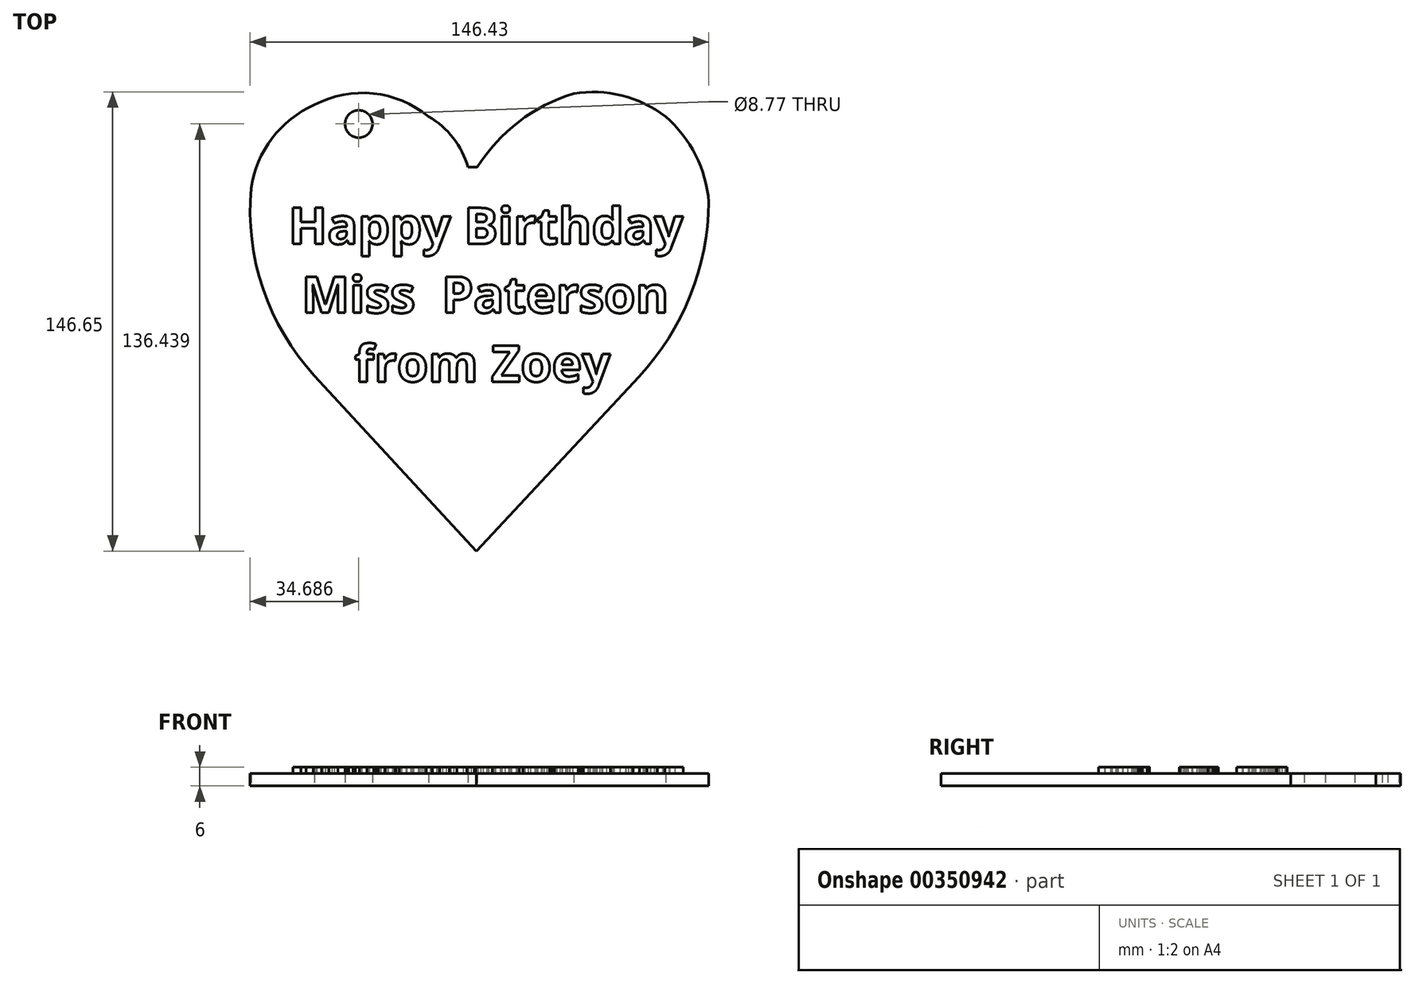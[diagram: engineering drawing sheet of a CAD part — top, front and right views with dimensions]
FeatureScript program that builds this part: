
annotation { "Feature Type Name" : "Feature", "Feature Type Description" : "" }
export const myFeature = defineFeature(function(context is Context, id is Id, definition is map)
    precondition{}
    {
        {
            var Q0;
            Q0=qCreatedBy(makeId("Top.planeOp"),FACE);
            var sketch = newSketch(context, id + "F0", { "sketchPlane" : qUnion([Q0])});
            skLineSegment(sketch, "E0", {"start": v(2.64, -78.33) * mm, "end": v(54.56, -22.56) * mm});
            skLineSegment(sketch, "E1", {"start": v(2.64, -78.33) * mm, "end": v(-49, -22.3) * mm});
            skArc(sketch, "E2", {"start": v(-69.24, 37.55) * mm, "mid": v(-65.47, 5.48) * mm, "end": v(-49, -22.3) * mm});
            skArc(sketch, "E3", {"start": v(-49, 64.25) * mm, "mid": v(-62.57, 53.52) * mm, "end": v(-69.24, 37.55) * mm});
            skArc(sketch, "E4", {"start": v(-12.62, 60.44) * mm, "mid": v(-30.23, 67.85) * mm, "end": v(-49, 64.25) * mm});
            skArc(sketch, "E5", {"start": v(0, 44.3) * mm, "mid": v(-4.71, 53.62) * mm, "end": v(-12.62, 60.44) * mm});
            skLineSegment(sketch, "E6", {"start": v(0, 44.3) * mm, "end": v(2.93, 44.3) * mm});
            skArc(sketch, "E7", {"start": v(33.73, 67.8) * mm, "mid": v(16.2, 58.84) * mm, "end": v(2.93, 44.3) * mm});
            skArc(sketch, "E8", {"start": v(63.07, 60.47) * mm, "mid": v(49.16, 67.19) * mm, "end": v(33.73, 67.8) * mm});
            skArc(sketch, "E9", {"start": v(76.86, 33.18) * mm, "mid": v(72.63, 48.18) * mm, "end": v(63.07, 60.47) * mm});
            skArc(sketch, "E10", {"start": v(54.56, -22.56) * mm, "mid": v(70.91, 3.23) * mm, "end": v(76.86, 33.18) * mm});
            skCircle(sketch, "E11", {"center": v(-34.88, 58.1) * mm, "radius": 4.39 * mm});
            skSolve(sketch);
        }
        {
            var Q0;
            Q0=qSketchRegion(id+"F0",true);
            extrude(context, id + "F1", {"entities" : qUnion([Q0]), "depth" : 4 * mm});
        }
        {
            var Q0;
            Q0=makeQuery(id+"F1.opExtrude","CAP_FACE",FACE,{"disambiguationData":[OSD([sQuery(id+"F0.wireOp",EDGE,"E0"),sQuery(id+"F0.wireOp",EDGE,"E1"),sQuery(id+"F0.wireOp",EDGE,"E2"),sQuery(id+"F0.wireOp",EDGE,"E3"),sQuery(id+"F0.wireOp",EDGE,"E4"),sQuery(id+"F0.wireOp",EDGE,"E5"),sQuery(id+"F0.wireOp",EDGE,"E6"),sQuery(id+"F0.wireOp",EDGE,"E7"),sQuery(id+"F0.wireOp",EDGE,"E8"),sQuery(id+"F0.wireOp",EDGE,"E9"),sQuery(id+"F0.wireOp",EDGE,"E10")])],"isStart":false});
            var sketch = newSketch(context, id + "F2", { "sketchPlane" : qUnion([Q0])});
            skText(sketch, "E12", { "text": "Happy Birthday\n Miss  Paterson\n     from Zoey", "fontName": "OpenSans-Bold.ttf"});
            const initialGuessF2  = {"E12": [-0.0573, 0.01978, 1, 0, 0.01164]};
            skSetInitialGuess(sketch, initialGuessF2);
            skSolve(sketch);
        }
        {
            var Q0;
            Q0=qSketchRegion(id+"F2",true);
            extrude(context, id + "F3", {"entities" : qUnion([Q0]), "operationType" : NewBodyOperationType.ADD, "depth" : 2 * mm});
        }
    });
